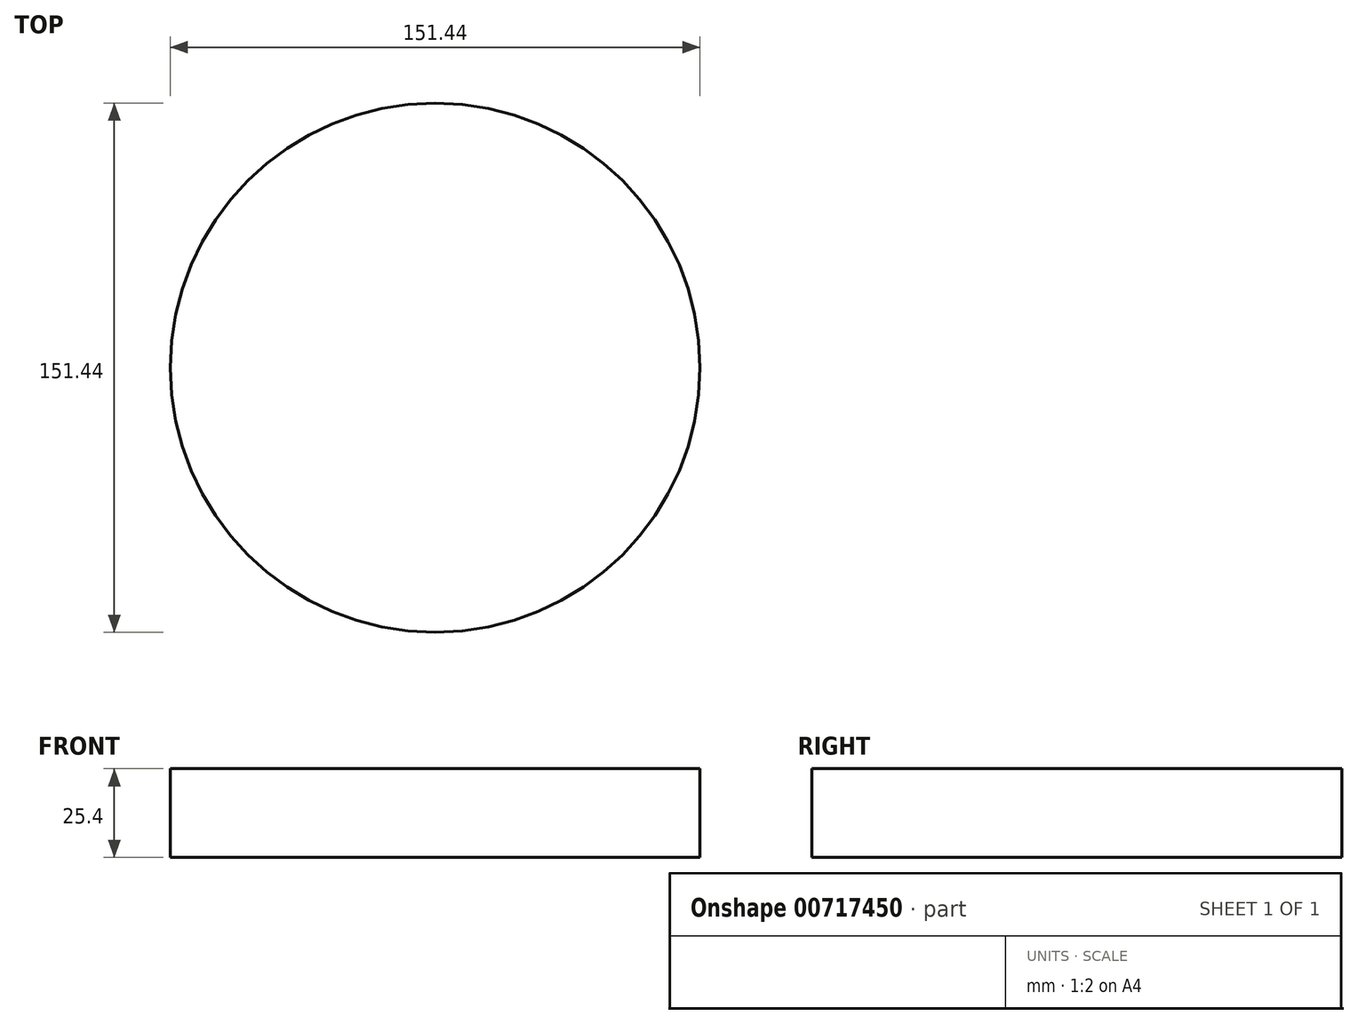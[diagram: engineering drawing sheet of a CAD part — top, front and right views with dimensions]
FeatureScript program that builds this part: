
annotation { "Feature Type Name" : "Feature", "Feature Type Description" : "" }
export const myFeature = defineFeature(function(context is Context, id is Id, definition is map)
    precondition{}
    {
        {
            var Q0;
            Q0=qCreatedBy(makeId("Top.planeOp"),FACE);
            var sketch = newSketch(context, id + "F0", { "sketchPlane" : qUnion([Q0])});
            skCircle(sketch, "E0", {"center": v(0, 0) * mm, "radius": 75.72 * mm});
            skSolve(sketch);
        }
        {
            var Q0;
            Q0=makeQuery(id+"F0.imprint","IMPRINT",FACE,{"disambiguationData":[TD([[makeQuery(id+"F0.imprint","IMPRINT",EDGE,{"derivedFrom":sQuery(id+"F0.wireOp",EDGE,"E0")}),1.0]])]});
            extrude(context, id + "F1", {"entities" : qUnion([Q0]), "depth" : 25.4 * mm, "offsetDistance" : 25.4 * mm});
        }
    });
